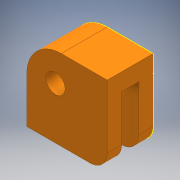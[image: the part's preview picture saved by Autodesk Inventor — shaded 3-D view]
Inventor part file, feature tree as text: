
AUTODESK INVENTOR PART (.ipt)
format: ipt  version: 2017 (Build 210142000, 142)  size: 167,936 bytes
history: native  units: mm
features: sketch x5, extrude x4, plane x1, fillet x1, projected_geometry x1
ambient origin geometry x8: Origin, YZ Plane, XZ Plane, XY Plane, X Axis, Y Axis, Z Axis, Center Point
bodies: Solid1 (feature_tree)
feature tree (12):
  extrude  "Extrusion1"  Depth=3.0mm
  extrude  "Extrusion2"  Depth=3.0mm
  plane  "Work Plane1"
  extrude  "Extrusion3"  Depth=8.0mm TaperAngle=0.0deg
  sketch  "Sketch4"  dims[d7=2.5mm d8=0.0mm d9=3.0mm d10=2.5mm d11=0.0mm]
  extrude  "Extrusion4"  Depth=3.0mm
  fillet  "Fillet2"  Radius=2.5mm
  sketch  "Sketch1"  dims[d0=3.0mm d1=3.0mm]
  sketch  "Sketch2"  dims[d2=8.0mm d3=3.0mm]
  sketch  "Sketch3"  dims[d4=8.0mm d5=8.0mm d6=0.0mm]
  projected_geometry  "Projected Loop1"
  sketch  "Sketch5"  dims[d21=3.333333mm d22=3.333333mm d23=3.333333mm d24=2.5mm d25=0.0mm d26=0.25mm]
